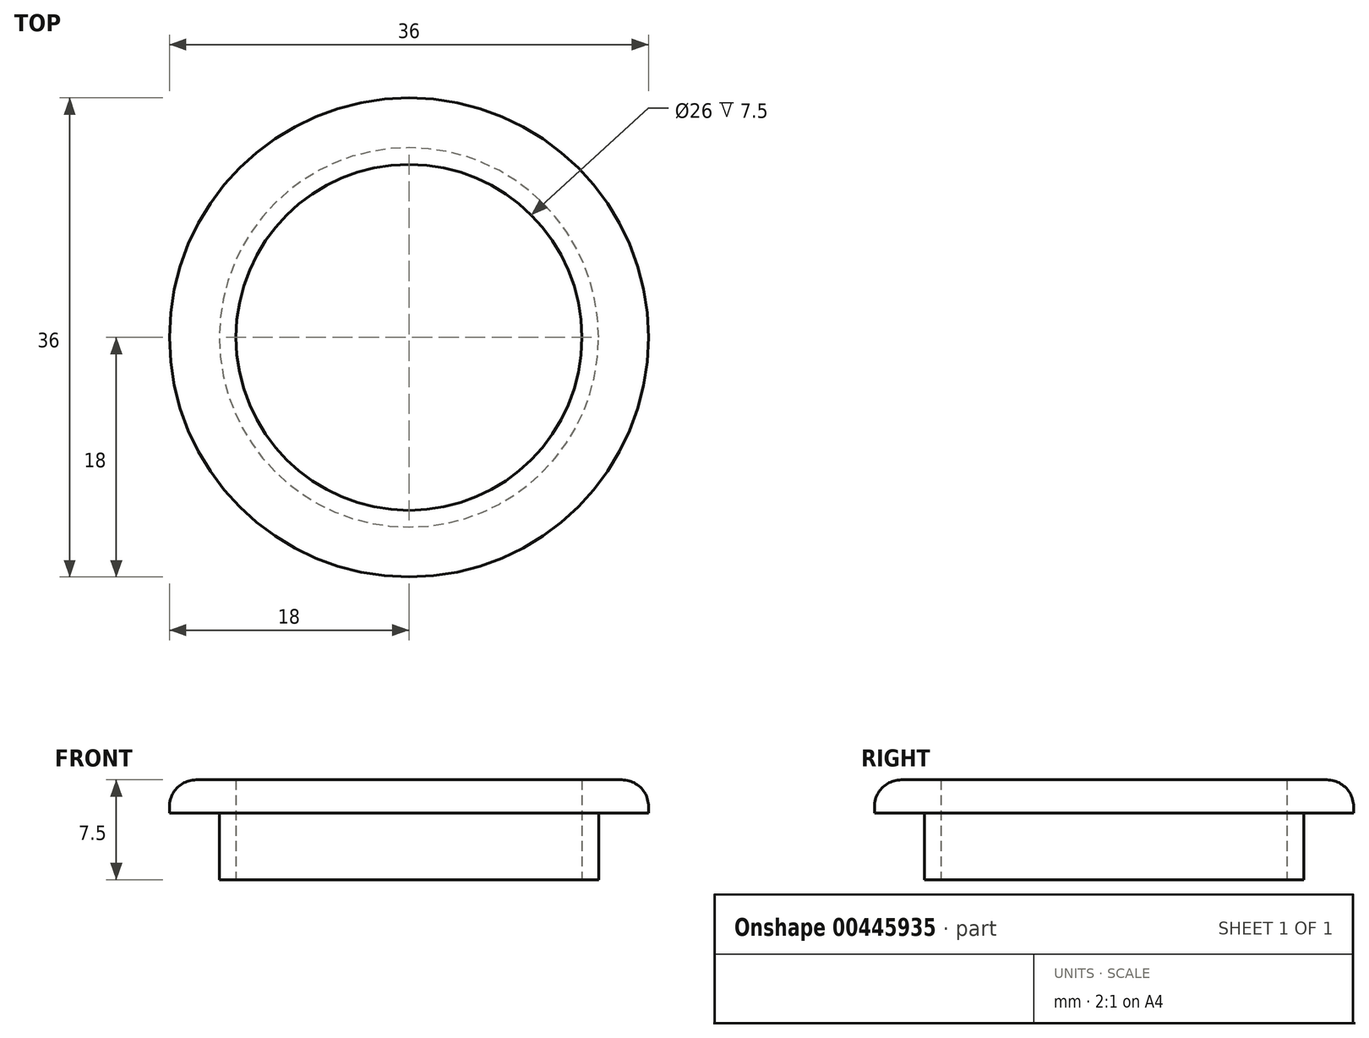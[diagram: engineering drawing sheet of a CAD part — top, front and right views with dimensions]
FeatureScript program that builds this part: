
annotation { "Feature Type Name" : "Feature", "Feature Type Description" : "" }
export const myFeature = defineFeature(function(context is Context, id is Id, definition is map)
    precondition{}
    {
        {
            var Q0;
            Q0=qCreatedBy(makeId("Top.planeOp"),FACE);
            var sketch = newSketch(context, id + "F0", { "sketchPlane" : qUnion([Q0])});
            skCircle(sketch, "E0", {"center": v(0, 0) * mm, "radius": 13 * mm});
            skCircle(sketch, "E1", {"center": v(0, 0) * mm, "radius": 18 * mm});
            skSolve(sketch);
        }
        {
            var Q0;
            Q0 = qSketchRegion(id + "F0", true);
            extrude(context, id + "F1", {"entities" : qUnion([Q0]), "depth" : 2.5 * mm});
        }
        {
            var Q0;
            Q0=makeQuery(id+"F1.opExtrude","CAP_FACE",FACE,{"disambiguationData":[OSD([sQuery(id+"F0.wireOp",EDGE,"E0"),sQuery(id+"F0.wireOp",EDGE,"E1")])],"isStart":true});
            var sketch = newSketch(context, id + "F2", { "sketchPlane" : qUnion([Q0])});
            skCircle(sketch, "E2", {"center": v(0, 0) * mm, "radius": 13 * mm});
            skCircle(sketch, "E3", {"center": v(0, 0) * mm, "radius": 14.25 * mm});
            skSolve(sketch);
        }
        {
            var Q0;
            Q0 = qSketchRegion(id + "F2", true);
            extrude(context, id + "F3", {"entities" : qUnion([Q0]), "operationType" : NewBodyOperationType.ADD, "depth" : 5 * mm});
        }
        {
            var Q0;
            Q0=makeQuery(id+"F1.opExtrude","CAP_EDGE",EDGE,{"disambiguationData":[OSD([sQuery(id+"F0.wireOp",EDGE,"E1")])],"isStart":false});
            fillet(context, id + "F4", {"entities" : qUnion([Q0]), "radius" : 2 * mm, "tangentPropagation" : true, "allowEdgeOverflow" : false});
        }
    });
